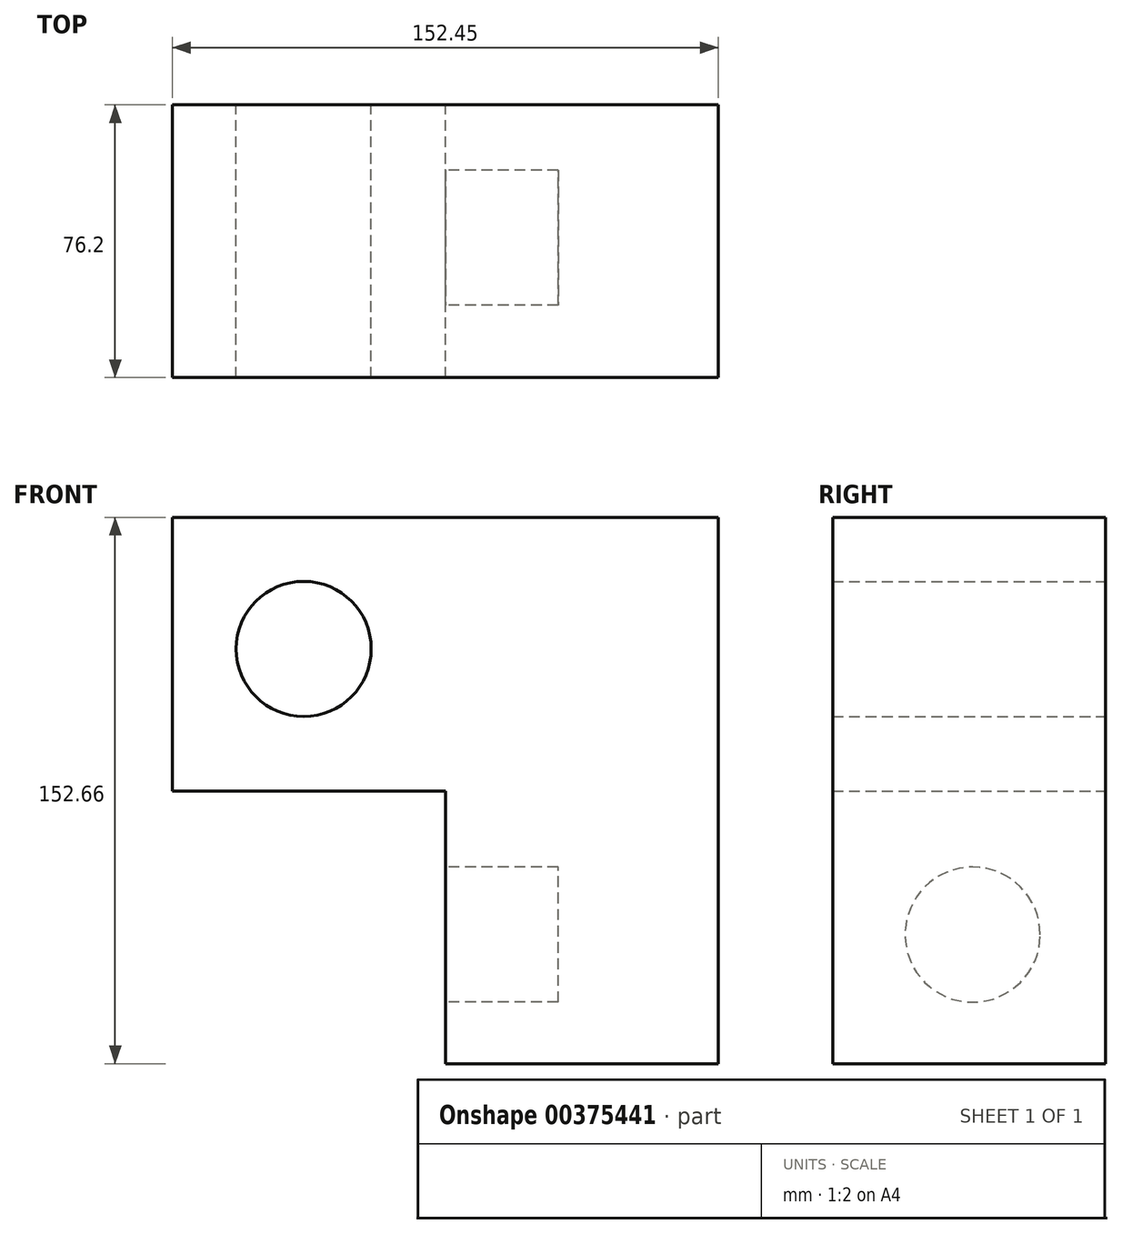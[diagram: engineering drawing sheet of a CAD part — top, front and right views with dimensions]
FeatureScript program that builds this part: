
annotation { "Feature Type Name" : "Feature", "Feature Type Description" : "" }
export const myFeature = defineFeature(function(context is Context, id is Id, definition is map)
    precondition{}
    {
        {
            var Q0;
            Q0=qCreatedBy(makeId("Front.planeOp"),FACE);
            var sketch = newSketch(context, id + "F0", { "sketchPlane" : qUnion([Q0])});
            skLineSegment(sketch, "E0.bottom", {"start": v(-76.26, 76.5) * mm, "end": v(76.19, 76.5) * mm});
            skLineSegment(sketch, "E0.top", {"start": v(-76.26, 0) * mm, "end": v(76.19, 0) * mm});
            skLineSegment(sketch, "E0.left", {"start": v(-76.26, 76.5) * mm, "end": v(-76.26, 0) * mm});
            skLineSegment(sketch, "E0.right", {"start": v(76.19, 76.5) * mm, "end": v(76.19, 0) * mm});
            skLineSegment(sketch, "E1.bottom", {"start": v(76.19, -76.16) * mm, "end": v(0, -76.16) * mm});
            skLineSegment(sketch, "E1.left", {"start": v(76.19, -76.16) * mm, "end": v(76.19, 0) * mm});
            skLineSegment(sketch, "E1.right", {"start": v(0, -76.16) * mm, "end": v(0, 0) * mm});
            skCircle(sketch, "E2", {"center": v(-39.62, 39.7) * mm, "radius": 18.88 * mm});
            skSolve(sketch);
        }
        {
            var Q0;
            Q0=makeQuery(id+"F0.imprint","IMPRINT",FACE,{"disambiguationData":[TD([[makeQuery(id+"F0.imprint","IMPRINT",EDGE,{"derivedFrom":sQuery(id+"F0.wireOp",EDGE,"E0.bottom")}),-1.0]])]});
            var Q1;
            Q1 = qSketchRegion(id + "F0", true);
            extrude(context, id + "F1", {"entities" : qUnion([Q0, Q1]), "depth" : 76.2 * mm});
        }
        {
            var Q0;
            Q0=qCreatedBy(makeId("Right.planeOp"),FACE);
            var sketch = newSketch(context, id + "F2", { "sketchPlane" : qUnion([Q0])});
            skCircle(sketch, "E3", {"center": v(-37.09, -40.11) * mm, "radius": 18.88 * mm});
            skSolve(sketch);
        }
        {
            var Q0;
            Q0 = qSketchRegion(id + "F2", true);
            extrude(context, id + "F3", {"entities" : qUnion([Q0]), "operationType" : NewBodyOperationType.REMOVE, "depth" : 31.5 * mm});
        }
    });
